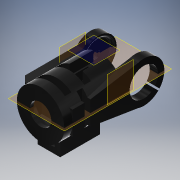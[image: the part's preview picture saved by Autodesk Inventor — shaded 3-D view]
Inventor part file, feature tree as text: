
AUTODESK INVENTOR PART (.ipt)
format: ipt  version: 2018 (Build 220112000, 112)  size: 693,248 bytes
history: native  units: mm
features: extrude x36, sketch x35, other x17, move_body x11, direct_edit x8, plane x5, fillet x1, chamfer x1
ambient origin geometry x8: Origin, YZ Plane, XZ Plane, XY Plane, X Axis, Y Axis, Z Axis, Center Point
bodies: Body1 (feature_tree), Body2 (feature_tree), Body3 (feature_tree), Body4 (feature_tree), Body5 (feature_tree), Body6 (feature_tree), Body7 (feature_tree)
feature tree (114):
  other  "Sólido1"
  extrude  "Extrusión1"  Depth=20.0mm
  plane  "Plano de trabajo1"
  plane  "Plano de trabajo2"
  extrude  "Extrusión8"  Depth=24.5mm
  plane  "Plano de trabajo5"
  plane  "Plano de trabajo6"
  extrude  "Extrusión12"  Depth=5.0mm TaperAngle=0.0deg
  extrude  "Extrusión13"  Depth=3.0mm
  extrude  "Extrusión14"  Depth=24.5mm
  extrude  "Extrusión15"  Depth=5.0mm
  extrude  "Extrusión16"  Depth=4.0mm
  extrude  "Extrusión23"  Depth=20.0mm
  extrude  "Extrusión27"  Depth=10.0mm
  extrude  "Extrusión28"  Depth=25.0mm TaperAngle=0.0deg
  extrude  "Extrusión29"  Depth=20.0mm TaperAngle=0.0deg
  extrude  "Extrusion31"  Depth=5.0mm
  extrude  "Extrusion32"  Depth=5.0mm TaperAngle=0.0deg
  extrude  "Extrusion34"  Depth=1.0mm
  extrude  "Extrusion37"  Depth=5.0mm TaperAngle=0.0deg
  extrude  "Extrusion38"  Depth=6.5mm
  extrude  "Extrusion39"  Depth=5.0mm
  extrude  "Extrusion40"  Depth=3.0mm
  direct_edit  "Direct Edit1"
  direct_edit  "Direct Edit2"
  direct_edit  "Direct Edit3"
  direct_edit  "Direct Edit4"
  extrude  "Extrusion41"  Depth=23.5mm
  extrude  "Extrusion42"  Depth=17.0mm TaperAngle=0.0deg
  direct_edit  "Direct Edit5"
  direct_edit  "Direct Edit6"
  direct_edit  "Direct Edit7"
  fillet  "Fillet6"  Radius=5.0mm
  direct_edit  "Direct Edit9"
  extrude  "Extrusión45"  Depth=5.0mm TaperAngle=0.0deg
  extrude  "Extrusión46"  Depth=2.0mm
  other  "Edición directa11"
  extrude  "Extrusión47"  Depth=1.0mm
  other  "Edición directa12"
  other  "Edición directa13"
  other  "Edición directa14"
  other  "Edición directa15"
  other  "Edición directa16"
  extrude  "Extrusión48"  Depth=7.0mm TaperAngle=0.0deg
  other  "Edición directa17"
  extrude  "Extrusión49"  TaperAngle=0.0deg  [1 undecoded]
  plane  "Plano de trabajo7"
  extrude  "Extrusión50"  TaperAngle=0.0deg  [1 undecoded]
  extrude  "Extrusión51"  Depth=1.0mm TaperAngle=0.0deg
  extrude  "Extrusión52"  Depth=7.0mm TaperAngle=0.0deg
  extrude  "Extrusión53"  Depth=7.0mm TaperAngle=0.0deg
  extrude  "Extrusión54"  Depth=2.0mm TaperAngle=0.0deg
  other  "Edición directa18"
  extrude  "Extrusión55"  Depth=2.0mm TaperAngle=0.0deg
  chamfer  "Chaflán5"  Distance=7.0mm
  extrude  "Extrusión56"  Depth=7.0mm TaperAngle=0.0deg
  extrude  "Extrusión57"  Depth=6.0mm
  extrude  "Extrusión58"  TaperAngle=0.0deg  [1 undecoded]
  extrude  "Extrusión59"  TaperAngle=0.0deg  [1 undecoded]
  extrude  "Extrusión60"  TaperAngle=0.0deg  [1 undecoded]
  sketch  "Boceto1"  dims[d0=40.0mm d1=20.0mm]
  sketch  "Boceto8"  dims[d2=5.0mm d3=0.0mm d28=24.5mm]
  sketch  "Boceto17"  dims[d30=10.0mm d31=0.0mm d53=5.0mm d54=0.0mm]
  sketch  "Boceto18"  dims[d55=3.0mm d56=0.0mm d58=6.3mm]
  sketch  "Boceto19"  dims[d59=8.0mm d60=0.0mm d61=24.5mm]
  sketch  "Boceto20"  dims[d62=5.0mm d63=0.0mm d64=1.6mm]
  sketch  "Boceto21"  dims[d65=2.0mm d66=0.0mm d99=4.0mm]
  sketch  "Boceto28"  dims[d100=25.0mm d101=0.0mm d117=20.0mm]
  sketch  "Boceto32"  dims[d118=90.0deg d119=10.0mm]
  sketch  "Boceto33"  dims[d120=5.0mm d121=25.0mm d122=0.0mm]
  sketch  "Boceto34"  dims[d123=10.0mm d124=0.0mm d125=20.0mm d126=0.0mm]
  sketch  "Sketch36"  dims[d130=10.0mm d131=0.0mm d133=5.0mm]
  sketch  "Sketch37"  dims[d134=5.0mm d135=5.0mm d136=0.0mm]
  sketch  "Sketch39"  dims[d154=8.0mm d155=1.0mm]
  sketch  "Sketch40"  dims[d156=1.0mm d157=5.0mm d158=0.0mm]
  sketch  "Sketch41"  dims[d165=7.0mm d166=0.0mm d167=6.5mm]
  sketch  "Sketch42"  dims[d168=6.5mm d169=5.0mm]
  sketch  "Sketch43"  dims[d170=5.0mm d171=3.0mm]
  sketch  "Sketch44"  dims[d172=3.0mm d173=23.5mm]
  sketch  "Boceto49"  dims[d174=5.0mm d175=17.0mm d176=0.0mm d180=5.0mm]
  sketch  "Boceto50"  dims[d181=5.0mm d182=5.0mm d183=0.0mm]
  sketch  "Boceto51"  dims[d186=2.0mm d187=2.0mm]
  sketch  "Boceto52"  dims[d188=3.0mm d189=1.0mm]
  sketch  "Boceto53"  dims[d190=6.0mm d191=7.0mm d192=0.0mm]
  sketch  "Boceto54"  dims[d193=0.0mm d194=0.0mm d195=-2.0mm d196=0.0mm d197=0.0mm d198=-2.0mm]
  sketch  "Boceto55"  dims[d199=0.0mm d200=0.0mm d201=2.0mm d202=0.0mm d203=0.0mm d204=-1.0mm]
  sketch  "Boceto56"  dims[d205=0.0mm d206=0.0mm d207=-1.0mm d208=0.0mm d209=0.0mm d210=1.0mm]
  sketch  "Boceto57"  dims[d211=3.5mm d212=0.0mm d222=7.0mm d223=0.0mm]
  sketch  "Boceto58"  dims[d224=0.0mm d225=0.0mm d226=-3.0mm d227=0.0mm d228=0.0mm d229=7.0mm]
  sketch  "Boceto59"  dims[d230=0.0mm d231=0.0mm d232=-3.0mm d233=0.0mm d234=0.0mm d235=2.0mm]
  sketch  "Boceto60"  dims[d242=2.0mm d243=0.0mm d244=0.0mm d245=9.75mm]
  sketch  "Boceto61"  dims[d262=24.0mm d263=7.0mm d264=0.0mm]
  sketch  "Boceto62"  dims[d266=2.0mm d267=7.0mm d268=0.0mm]
  sketch  "Boceto63"  dims[d269=0.0mm d270=0.0mm d271=13.0mm d272=6.0mm]
  sketch  "Boceto64"  dims[d273=31.0mm d274=0.0mm d275=0.0mm d276=0.0mm d277=-25.0mm d278=0.0mm d279=0.0mm d280=-2.9mm d281=0.0mm d282=0.0mm d283=-2.9mm d284=0.0mm d285=0.0mm d286=3.4mm d287=0.0mm d288=0.0mm d289=42.9mm d290=10.0mm d291=4.0mm d292=0.0mm d293=0.0mm d294=0.0mm d295=23.25mm d296=9.4mm d297=0.0mm d298=20.0mm d303=5.5mm d307=5.5mm d308=0.5mm d310=32.0mm d311=0.0mm d314=18.0mm d315=3.0mm d316=0.0mm d317=18.0mm d318=5.9mm d319=0.0mm d320=5.0mm d321=0.0mm d322=5.0mm d323=0.0mm d324=0.0mm d325=0.0mm d326=-7.0mm d329=5.0mm d330=4.0mm d331=90.0deg d332=10.0mm d333=5.0mm d334=0.0mm d335=5.0mm d336=2.0mm d337=45.0deg d338=15.0mm d340=5.0mm d342=180.0deg d343=5.0mm d344=7.0mm d345=0.0mm d348=7.0mm d349=0.0mm d350=5.0mm d351=0.0mm d352=5.0mm d353=0.0mm d355=0.5mm d356=180.0deg d357=20.0mm d358=0.0mm]
  move_body  "Move1"
  move_body  "Move2"
  move_body  "Move3"
  move_body  "Move4"
  move_body  "Move5"
  move_body  "Move6"
  move_body  "Move7"
  move_body  "Move8"
  move_body  "Move9"
  move_body  "Move10"
  move_body  "Move12"
  other  "Desplazar14"
  other  "Desplazar15"
  other  "Desplazar16"
  other  "Desplazar17"
  other  "Desplazar18"
  other  "Desplazar19"
  other  "Desplazar20"
  other  "Desplazar21"
note: 5 required parameter values undecoded (feature->parameter linkage not recoverable at this tier; creation-order binding heuristic only, values carry confidence <= 0.55)
